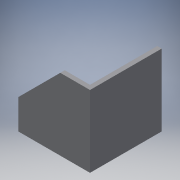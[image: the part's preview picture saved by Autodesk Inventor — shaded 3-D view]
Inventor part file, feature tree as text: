
AUTODESK INVENTOR PART (.ipt)
format: ipt  version: 2016 (Build 200138000, 138)  size: 130,560 bytes
history: native  units: in
note: dims shown in document units (in); Inventor stores cm internally (conversion verified against a paired STEP export)
features: extrude x4, sketch x4
ambient origin geometry x8: Origin, YZ Plane, XZ Plane, XY Plane, X Axis, Y Axis, Z Axis, Center Point
bodies: Solid1 (feature_tree)
feature tree (8):
  extrude  "Extrusion1"  Depth=2.0in
  extrude  "Extrusion2"  TaperAngle=135.0deg  [1 undecoded]
  extrude  "Extrusion3"  Depth=0.125in
  extrude  "Extrusion4"  Depth=0.125in
  sketch  "Sketch1"  dims[d0=2.0in d2=2.0in]
  sketch  "Sketch2"  dims[d3=2.0in d4=135.0deg]
  sketch  "Sketch3"  dims[d5=0.125in d6=0.0in d7=0.125in]
  sketch  "Sketch4"  dims[d8=2.0in d9=0.0in d10=0.2656in d11=0.2656in d12=0.546in d13=0.546in d14=0.5in d15=1.0in d16=0.125in d17=0.0in d18=0.656in d19=0.5in d20=0.5in d21=0.2656in d22=1.0in d23=0.125in d24=0.0in]
note: 1 required parameter value undecoded (feature->parameter linkage not recoverable at this tier; creation-order binding heuristic only, values carry confidence <= 0.55)
